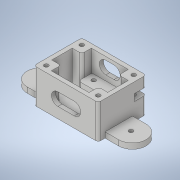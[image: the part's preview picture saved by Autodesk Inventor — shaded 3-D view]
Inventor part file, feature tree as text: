
AUTODESK INVENTOR PART (.ipt)
format: ipt  version: 2022 (Build 260153000, 153)  size: 336,384 bytes
history: native  units: mm
features: extrude x13, sketch x12, fillet x3, other x1, shell x1, chamfer x1
ambient origin geometry x8: Origin, YZ Plane, XZ Plane, XY Plane, X Axis, Y Axis, Z Axis, Center Point
bodies: Body1 (feature_tree)
feature tree (31):
  other  "Sólido1"
  extrude  "Extrusão1"  Depth=35.0mm
  shell  "Casca1"  Thickness=25.0mm
  extrude  "Extrusão2"  Depth=9.3mm
  extrude  "Extrusão3"  Depth=9.3mm
  fillet  "Arredondamento1"  Radius=12.0mm
  fillet  "Arredondamento2"  Radius=17.5mm
  extrude  "Extrusão26"  Depth=7.0mm
  extrude  "Extrusão28"  Depth=7.0mm
  fillet  "Arredondamento9"  Radius=7.0mm
  extrude  "Extrusão29"  Depth=7.0mm
  extrude  "Extrusão32"  Depth=7.0mm
  extrude  "Extrusão33"  Depth=26.0mm
  extrude  "Extrusão34"  Depth=0.5mm
  extrude  "Extrusão35"  Depth=2.0mm
  extrude  "Extrusão36"  Depth=4.0mm
  extrude  "Extrusão37"  Depth=20.0mm TaperAngle=0.0deg
  chamfer  "Chanfro5"  Distance=20.0mm
  extrude  "Extrusão39"  Depth=10.0mm
  sketch  "Esboço1"  dims[d0=47.0mm d1=35.0mm d2=25.0mm d3=0.0mm]
  sketch  "Esboço2"  dims[d4=3.0mm d5=9.3mm]
  sketch  "Esboço3"  dims[d6=12.5mm d7=9.3mm d8=12.0mm d9=17.5mm]
  sketch  "Esboço35"  dims[d10=10.0mm d11=0.0mm d12=7.0mm]
  sketch  "Esboço37"  dims[d13=7.0mm d14=7.0mm d15=7.0mm]
  sketch  "Esboço38"  dims[d16=6.7mm d17=7.0mm]
  sketch  "Esboço40"  dims[d18=6.7mm d19=7.0mm]
  sketch  "Esboço42"  dims[d20=22.0mm d21=0.0mm d33=26.0mm]
  sketch  "Esboço44"  dims[d34=10.0mm d35=0.5mm]
  sketch  "Esboço46"  dims[d63=2.0mm d64=2.0mm]
  sketch  "Esboço47"  dims[d160=20.0mm d161=4.0mm]
  sketch  "Esboço50"  dims[d162=5.0mm d163=20.0mm d164=0.0mm d170=20.0mm d171=0.0mm d172=10.0mm d173=3.0mm d174=3.0mm d175=3.0mm d176=10.0mm d177=9.0mm d178=10.0mm d179=9.0mm d180=10.0mm d181=9.0mm d182=20.0mm d183=0.0mm d222=8.5mm d223=5.0mm d224=8.5mm d225=0.0mm d226=3.01mm d227=4.5mm d228=4.5mm d229=20.0mm d231=26.0mm d232=20.0mm d234=38.0mm d237=20.0mm d238=0.0mm d239=8.5mm d240=5.0mm d241=7.5mm d242=7.5mm d243=8.5mm d244=0.0mm d247=4.5mm d248=0.0mm d249=2.0mm d250=0.0mm d251=3.01mm d252=3.01mm d253=3.01mm d254=0.0mm d255=1.5mm d256=2.0mm d257=45.0deg d264=9.3mm d265=18.0mm d266=9.3mm d267=6.0mm d268=20.5mm d269=10.0mm d270=0.0mm]
